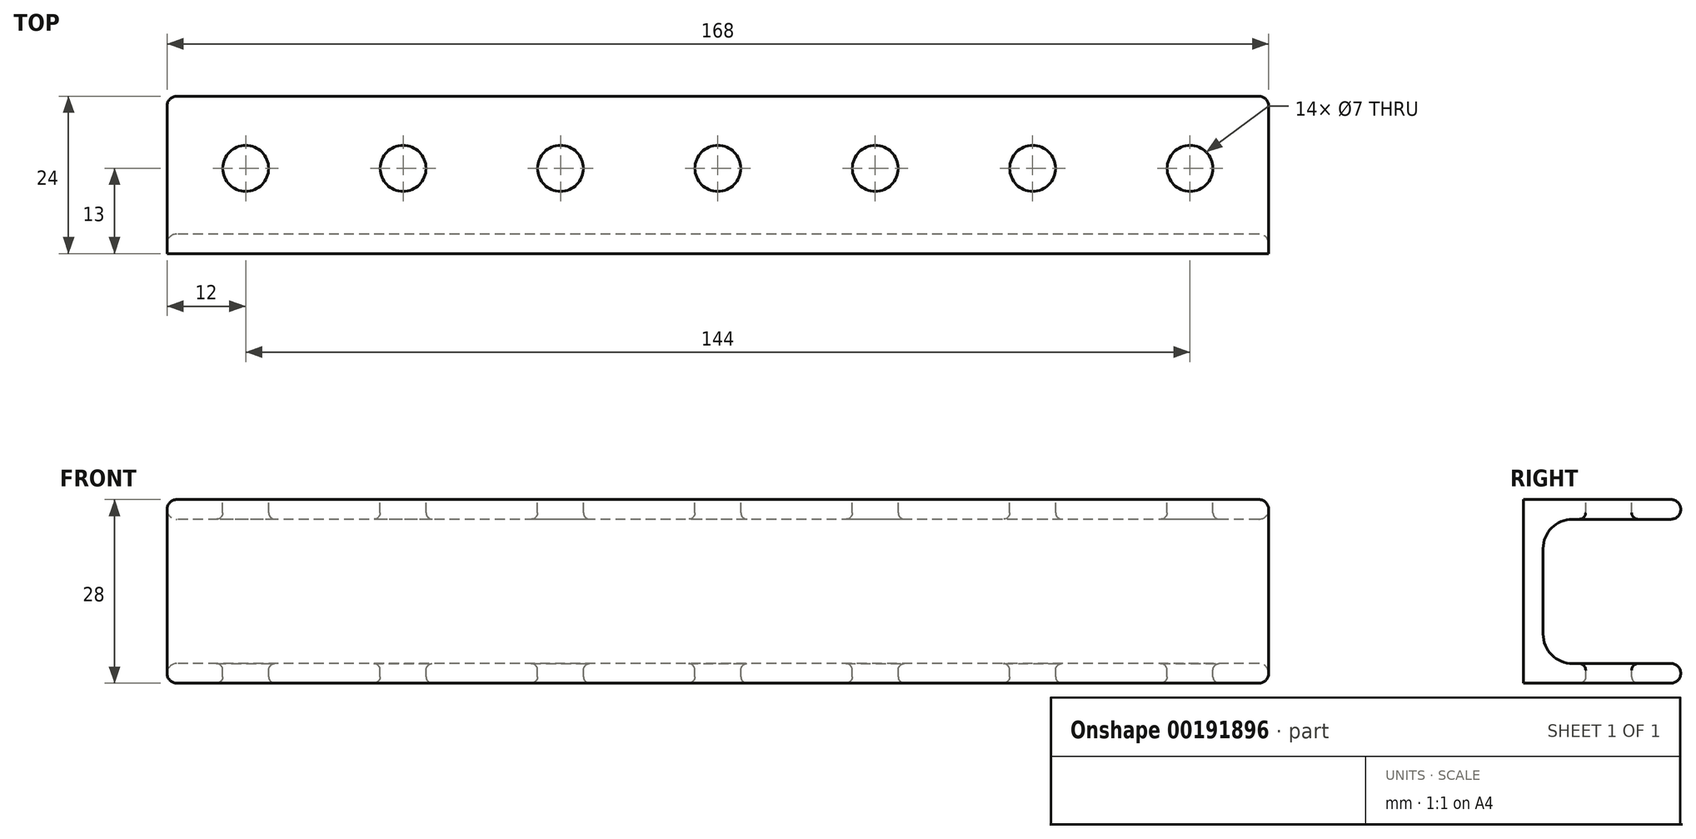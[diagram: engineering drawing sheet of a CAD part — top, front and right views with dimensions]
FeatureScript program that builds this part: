
annotation { "Feature Type Name" : "Feature", "Feature Type Description" : "" }
export const myFeature = defineFeature(function(context is Context, id is Id, definition is map)
    precondition{}
    {
        {
            var Q0;
            Q0=qCreatedBy(makeId("Right.planeOp"),FACE);
            var sketch = newSketch(context, id + "F0", { "sketchPlane" : qUnion([Q0])});
            skLineSegment(sketch, "E0", {"start": v(0, 28) * mm, "end": v(0, 0) * mm});
            skLineSegment(sketch, "E1", {"start": v(0, 0) * mm, "end": v(24, 0) * mm});
            skLineSegment(sketch, "E2", {"start": v(24, 0) * mm, "end": v(24, 3) * mm});
            skLineSegment(sketch, "E3", {"start": v(24, 3) * mm, "end": v(3, 3) * mm});
            skLineSegment(sketch, "E4", {"start": v(3, 3) * mm, "end": v(3, 25) * mm});
            skLineSegment(sketch, "E5", {"start": v(3, 25) * mm, "end": v(24, 25) * mm});
            skLineSegment(sketch, "E6", {"start": v(24, 25) * mm, "end": v(24, 28) * mm});
            skLineSegment(sketch, "E7", {"start": v(24, 28) * mm, "end": v(0, 28) * mm});
            skSolve(sketch);
        }
        {
            var Q0;
            Q0=makeQuery(id+"F0.imprint","IMPRINT",FACE,{"disambiguationData":[TD([[makeQuery(id+"F0.imprint","IMPRINT",EDGE,{"derivedFrom":sQuery(id+"F0.wireOp",EDGE,"E0")}),1.0]])]});
            extrude(context, id + "F1", {"entities" : qUnion([Q0]), "depth" : 168 * mm});
        }
        {
            var Q0;
            Q0=makeQuery(id+"F1.opExtrude","SWEPT_FACE",FACE,{"disambiguationData":[OSD([sQuery(id+"F0.wireOp",EDGE,"E7")])]});
            var sketch = newSketch(context, id + "F2", { "sketchPlane" : qUnion([Q0])});
            skCircle(sketch, "E8", {"center": v(12, 13) * mm, "radius": 3.5 * mm});
            skCircle(sketch, "E9.1.0.0", {"center": v(36, 13) * mm, "radius": 3.5 * mm});
            skCircle(sketch, "E9.2.0.0", {"center": v(60, 13) * mm, "radius": 3.5 * mm});
            skCircle(sketch, "E9.3.0.0", {"center": v(84, 13) * mm, "radius": 3.5 * mm});
            skCircle(sketch, "E9.4.0.0", {"center": v(108, 13) * mm, "radius": 3.5 * mm});
            skCircle(sketch, "E9.5.0.0", {"center": v(132, 13) * mm, "radius": 3.5 * mm});
            skCircle(sketch, "E9.6.0.0", {"center": v(156, 13) * mm, "radius": 3.5 * mm});
            skLineSegment(sketch, "E9.direction1", {"start": v(12, 13) * mm, "end": v(36, 13) * mm, "construction": true});
            skSolve(sketch);
        }
        {
            var Q0;
            Q0=makeQuery(id+"F2.imprint","IMPRINT",FACE,{"disambiguationData":[TD([[makeQuery(id+"F2.imprint","IMPRINT",EDGE,{"derivedFrom":sQuery(id+"F2.wireOp",EDGE,"E8")}),1.0]])]});
            var Q1;
            Q1=makeQuery(id+"F2.imprint","IMPRINT",FACE,{"disambiguationData":[TD([[makeQuery(id+"F2.imprint","IMPRINT",EDGE,{"derivedFrom":sQuery(id+"F2.wireOp",EDGE,"E9.1.0.0")}),1.0]])]});
            var Q2;
            Q2=makeQuery(id+"F2.imprint","IMPRINT",FACE,{"disambiguationData":[TD([[makeQuery(id+"F2.imprint","IMPRINT",EDGE,{"derivedFrom":sQuery(id+"F2.wireOp",EDGE,"E9.2.0.0")}),1.0]])]});
            var Q3;
            Q3=makeQuery(id+"F2.imprint","IMPRINT",FACE,{"disambiguationData":[TD([[makeQuery(id+"F2.imprint","IMPRINT",EDGE,{"derivedFrom":sQuery(id+"F2.wireOp",EDGE,"E9.3.0.0")}),1.0]])]});
            var Q4;
            Q4=makeQuery(id+"F2.imprint","IMPRINT",FACE,{"disambiguationData":[TD([[makeQuery(id+"F2.imprint","IMPRINT",EDGE,{"derivedFrom":sQuery(id+"F2.wireOp",EDGE,"E9.4.0.0")}),1.0]])]});
            var Q5;
            Q5=makeQuery(id+"F2.imprint","IMPRINT",FACE,{"disambiguationData":[TD([[makeQuery(id+"F2.imprint","IMPRINT",EDGE,{"derivedFrom":sQuery(id+"F2.wireOp",EDGE,"E9.5.0.0")}),1.0]])]});
            var Q6;
            Q6=makeQuery(id+"F2.imprint","IMPRINT",FACE,{"disambiguationData":[TD([[makeQuery(id+"F2.imprint","IMPRINT",EDGE,{"derivedFrom":sQuery(id+"F2.wireOp",EDGE,"E9.6.0.0")}),1.0]])]});
            extrude(context, id + "F3", {"entities" : qUnion([Q0, Q1, Q2, Q3, Q4, Q5, Q6]), "operationType" : NewBodyOperationType.REMOVE, "endBound" : BoundingType.THROUGH_ALL, "oppositeDirection" : true, "depth" : 25 * mm});
        }
        {
            var Q0;
            Q0=makeQuery(id+"F1.opExtrude","SWEPT_EDGE",EDGE,{"disambiguationData":[OSD([sQuery(id+"F0.wireOp",EDGE,"E3"),sQuery(id+"F0.wireOp",EDGE,"E4")])]});
            var Q1;
            Q1=makeQuery(id+"F1.opExtrude","SWEPT_EDGE",EDGE,{"disambiguationData":[OSD([sQuery(id+"F0.wireOp",EDGE,"E4"),sQuery(id+"F0.wireOp",EDGE,"E5")])]});
            fillet(context, id + "F4", {"entities" : qUnion([Q0, Q1]), "radius" : 4.5 * mm, "tangentPropagation" : true, "allowEdgeOverflow" : false});
        }
        {
            var Q0;
            Q0=makeQuery(id+"F1.opExtrude","SWEPT_EDGE",EDGE,{"disambiguationData":[OSD([sQuery(id+"F0.wireOp",EDGE,"E2"),sQuery(id+"F0.wireOp",EDGE,"E3")])]});
            var Q1;
            Q1=makeQuery(id+"F1.opExtrude","SWEPT_EDGE",EDGE,{"disambiguationData":[OSD([sQuery(id+"F0.wireOp",EDGE,"E5"),sQuery(id+"F0.wireOp",EDGE,"E6")])]});
            var Q2;
            Q2=makeQuery(id+"F1.opExtrude","SWEPT_EDGE",EDGE,{"disambiguationData":[OSD([sQuery(id+"F0.wireOp",EDGE,"E6"),sQuery(id+"F0.wireOp",EDGE,"E7")])]});
            var Q3;
            Q3=makeQuery(id+"F1.opExtrude","SWEPT_EDGE",EDGE,{"disambiguationData":[OSD([sQuery(id+"F0.wireOp",EDGE,"E1"),sQuery(id+"F0.wireOp",EDGE,"E2")])]});
            var Q4;
            Q4=makeQuery(id+"F1.opExtrude","CAP_EDGE",EDGE,{"disambiguationData":[OSD([sQuery(id+"F0.wireOp",EDGE,"E2")])],"isStart":true});
            var Q5;
            Q5=makeQuery(id+"F1.opExtrude","CAP_EDGE",EDGE,{"disambiguationData":[OSD([sQuery(id+"F0.wireOp",EDGE,"E6")])],"isStart":true});
            var Q6;
            Q6=makeQuery(id+"F1.opExtrude","CAP_EDGE",EDGE,{"disambiguationData":[OSD([sQuery(id+"F0.wireOp",EDGE,"E2")])],"isStart":false});
            var Q7;
            Q7=makeQuery(id+"F1.opExtrude","CAP_EDGE",EDGE,{"disambiguationData":[OSD([sQuery(id+"F0.wireOp",EDGE,"E6")])],"isStart":false});
            var Q8;
            Q8=makeQuery(id+"F1.opExtrude","CAP_EDGE",EDGE,{"disambiguationData":[OSD([sQuery(id+"F0.wireOp",EDGE,"E1")])],"isStart":false});
            var Q9;
            Q9=makeQuery(id+"F1.opExtrude","CAP_EDGE",EDGE,{"disambiguationData":[OSD([sQuery(id+"F0.wireOp",EDGE,"E3")])],"isStart":false});
            var Q10;
            Q10=makeQuery(id+"F1.opExtrude","CAP_EDGE",EDGE,{"disambiguationData":[OSD([sQuery(id+"F0.wireOp",EDGE,"E7")])],"isStart":false});
            var Q11;
            Q11=makeQuery(id+"F1.opExtrude","CAP_EDGE",EDGE,{"disambiguationData":[OSD([sQuery(id+"F0.wireOp",EDGE,"E5")])],"isStart":true});
            var Q12;
            Q12=makeQuery(id+"F1.opExtrude","CAP_EDGE",EDGE,{"disambiguationData":[OSD([sQuery(id+"F0.wireOp",EDGE,"E7")])],"isStart":true});
            var Q13;
            Q13=makeQuery(id+"F1.opExtrude","CAP_EDGE",EDGE,{"disambiguationData":[OSD([sQuery(id+"F0.wireOp",EDGE,"E1")])],"isStart":true});
            fillet(context, id + "F5", {"entities" : qUnion([Q0, Q1, Q2, Q3, Q4, Q5, Q6, Q7, Q8, Q9, Q10, Q11, Q12, Q13]), "radius" : 1.5 * mm, "tangentPropagation" : true, "allowEdgeOverflow" : false});
        }
        {
            var Q0;
            Q0=makeQuery(id+"F3.boolean.opBoolean","COPY",EDGE,{"derivedFrom":makeQuery(id+"F3.opExtrude","CAP_EDGE",EDGE,{"disambiguationData":[OSD([sQuery(id+"F2.wireOp",EDGE,"E8")])],"isStart":true})});
            var Q1;
            Q1=makeQuery(id+"F3.boolean.opBoolean","COPY",EDGE,{"derivedFrom":makeQuery(id+"F3.opExtrude","CAP_EDGE",EDGE,{"disambiguationData":[OSD([sQuery(id+"F2.wireOp",EDGE,"E9.1.0.0")])],"isStart":true})});
            var Q2;
            Q2=makeQuery(id+"F3.boolean.opBoolean","INTERSECT",EDGE,{"derivedFrom":[makeQuery(id+"F1.opExtrude","SWEPT_FACE",FACE,{"disambiguationData":[OSD([sQuery(id+"F0.wireOp",EDGE,"E5")])]}),makeQuery(id+"F3.opExtrude","SWEPT_FACE",FACE,{"disambiguationData":[OSD([sQuery(id+"F2.wireOp",EDGE,"E8")])]})]});
            var Q3;
            Q3=makeQuery(id+"F3.boolean.opBoolean","INTERSECT",EDGE,{"derivedFrom":[makeQuery(id+"F1.opExtrude","SWEPT_FACE",FACE,{"disambiguationData":[OSD([sQuery(id+"F0.wireOp",EDGE,"E5")])]}),makeQuery(id+"F3.opExtrude","SWEPT_FACE",FACE,{"disambiguationData":[OSD([sQuery(id+"F2.wireOp",EDGE,"E9.1.0.0")])]})]});
            var Q4;
            Q4=makeQuery(id+"F3.boolean.opBoolean","COPY",EDGE,{"derivedFrom":makeQuery(id+"F3.opExtrude","CAP_EDGE",EDGE,{"disambiguationData":[OSD([sQuery(id+"F2.wireOp",EDGE,"E9.2.0.0")])],"isStart":true})});
            var Q5;
            Q5=makeQuery(id+"F3.boolean.opBoolean","INTERSECT",EDGE,{"derivedFrom":[makeQuery(id+"F1.opExtrude","SWEPT_FACE",FACE,{"disambiguationData":[OSD([sQuery(id+"F0.wireOp",EDGE,"E5")])]}),makeQuery(id+"F3.opExtrude","SWEPT_FACE",FACE,{"disambiguationData":[OSD([sQuery(id+"F2.wireOp",EDGE,"E9.2.0.0")])]})]});
            var Q6;
            Q6=makeQuery(id+"F3.boolean.opBoolean","COPY",EDGE,{"derivedFrom":makeQuery(id+"F3.opExtrude","CAP_EDGE",EDGE,{"disambiguationData":[OSD([sQuery(id+"F2.wireOp",EDGE,"E9.3.0.0")])],"isStart":true})});
            var Q7;
            Q7=makeQuery(id+"F3.boolean.opBoolean","INTERSECT",EDGE,{"derivedFrom":[makeQuery(id+"F1.opExtrude","SWEPT_FACE",FACE,{"disambiguationData":[OSD([sQuery(id+"F0.wireOp",EDGE,"E5")])]}),makeQuery(id+"F3.opExtrude","SWEPT_FACE",FACE,{"disambiguationData":[OSD([sQuery(id+"F2.wireOp",EDGE,"E9.3.0.0")])]})]});
            var Q8;
            Q8=makeQuery(id+"F3.boolean.opBoolean","COPY",EDGE,{"derivedFrom":makeQuery(id+"F3.opExtrude","CAP_EDGE",EDGE,{"disambiguationData":[OSD([sQuery(id+"F2.wireOp",EDGE,"E9.4.0.0")])],"isStart":true})});
            var Q9;
            Q9=makeQuery(id+"F3.boolean.opBoolean","INTERSECT",EDGE,{"derivedFrom":[makeQuery(id+"F1.opExtrude","SWEPT_FACE",FACE,{"disambiguationData":[OSD([sQuery(id+"F0.wireOp",EDGE,"E5")])]}),makeQuery(id+"F3.opExtrude","SWEPT_FACE",FACE,{"disambiguationData":[OSD([sQuery(id+"F2.wireOp",EDGE,"E9.4.0.0")])]})]});
            var Q10;
            Q10=makeQuery(id+"F3.boolean.opBoolean","COPY",EDGE,{"derivedFrom":makeQuery(id+"F3.opExtrude","CAP_EDGE",EDGE,{"disambiguationData":[OSD([sQuery(id+"F2.wireOp",EDGE,"E9.5.0.0")])],"isStart":true})});
            var Q11;
            Q11=makeQuery(id+"F3.boolean.opBoolean","INTERSECT",EDGE,{"derivedFrom":[makeQuery(id+"F1.opExtrude","SWEPT_FACE",FACE,{"disambiguationData":[OSD([sQuery(id+"F0.wireOp",EDGE,"E1")])]}),makeQuery(id+"F3.opExtrude","SWEPT_FACE",FACE,{"disambiguationData":[OSD([sQuery(id+"F2.wireOp",EDGE,"E8")])]})]});
            var Q12;
            Q12=makeQuery(id+"F3.boolean.opBoolean","INTERSECT",EDGE,{"derivedFrom":[makeQuery(id+"F1.opExtrude","SWEPT_FACE",FACE,{"disambiguationData":[OSD([sQuery(id+"F0.wireOp",EDGE,"E1")])]}),makeQuery(id+"F3.opExtrude","SWEPT_FACE",FACE,{"disambiguationData":[OSD([sQuery(id+"F2.wireOp",EDGE,"E9.1.0.0")])]})]});
            var Q13;
            Q13=makeQuery(id+"F3.boolean.opBoolean","INTERSECT",EDGE,{"derivedFrom":[makeQuery(id+"F1.opExtrude","SWEPT_FACE",FACE,{"disambiguationData":[OSD([sQuery(id+"F0.wireOp",EDGE,"E3")])]}),makeQuery(id+"F3.opExtrude","SWEPT_FACE",FACE,{"disambiguationData":[OSD([sQuery(id+"F2.wireOp",EDGE,"E9.1.0.0")])]})]});
            var Q14;
            Q14=makeQuery(id+"F3.boolean.opBoolean","INTERSECT",EDGE,{"derivedFrom":[makeQuery(id+"F1.opExtrude","SWEPT_FACE",FACE,{"disambiguationData":[OSD([sQuery(id+"F0.wireOp",EDGE,"E3")])]}),makeQuery(id+"F3.opExtrude","SWEPT_FACE",FACE,{"disambiguationData":[OSD([sQuery(id+"F2.wireOp",EDGE,"E8")])]})]});
            var Q15;
            Q15=makeQuery(id+"F3.boolean.opBoolean","INTERSECT",EDGE,{"derivedFrom":[makeQuery(id+"F1.opExtrude","SWEPT_FACE",FACE,{"disambiguationData":[OSD([sQuery(id+"F0.wireOp",EDGE,"E1")])]}),makeQuery(id+"F3.opExtrude","SWEPT_FACE",FACE,{"disambiguationData":[OSD([sQuery(id+"F2.wireOp",EDGE,"E9.2.0.0")])]})]});
            var Q16;
            Q16=makeQuery(id+"F3.boolean.opBoolean","INTERSECT",EDGE,{"derivedFrom":[makeQuery(id+"F1.opExtrude","SWEPT_FACE",FACE,{"disambiguationData":[OSD([sQuery(id+"F0.wireOp",EDGE,"E1")])]}),makeQuery(id+"F3.opExtrude","SWEPT_FACE",FACE,{"disambiguationData":[OSD([sQuery(id+"F2.wireOp",EDGE,"E9.3.0.0")])]})]});
            var Q17;
            Q17=makeQuery(id+"F3.boolean.opBoolean","INTERSECT",EDGE,{"derivedFrom":[makeQuery(id+"F1.opExtrude","SWEPT_FACE",FACE,{"disambiguationData":[OSD([sQuery(id+"F0.wireOp",EDGE,"E1")])]}),makeQuery(id+"F3.opExtrude","SWEPT_FACE",FACE,{"disambiguationData":[OSD([sQuery(id+"F2.wireOp",EDGE,"E9.4.0.0")])]})]});
            var Q18;
            Q18=makeQuery(id+"F3.boolean.opBoolean","INTERSECT",EDGE,{"derivedFrom":[makeQuery(id+"F1.opExtrude","SWEPT_FACE",FACE,{"disambiguationData":[OSD([sQuery(id+"F0.wireOp",EDGE,"E1")])]}),makeQuery(id+"F3.opExtrude","SWEPT_FACE",FACE,{"disambiguationData":[OSD([sQuery(id+"F2.wireOp",EDGE,"E9.5.0.0")])]})]});
            var Q19;
            Q19=makeQuery(id+"F3.boolean.opBoolean","INTERSECT",EDGE,{"derivedFrom":[makeQuery(id+"F1.opExtrude","SWEPT_FACE",FACE,{"disambiguationData":[OSD([sQuery(id+"F0.wireOp",EDGE,"E1")])]}),makeQuery(id+"F3.opExtrude","SWEPT_FACE",FACE,{"disambiguationData":[OSD([sQuery(id+"F2.wireOp",EDGE,"E9.6.0.0")])]})]});
            var Q20;
            Q20=makeQuery(id+"F3.boolean.opBoolean","INTERSECT",EDGE,{"derivedFrom":[makeQuery(id+"F1.opExtrude","SWEPT_FACE",FACE,{"disambiguationData":[OSD([sQuery(id+"F0.wireOp",EDGE,"E3")])]}),makeQuery(id+"F3.opExtrude","SWEPT_FACE",FACE,{"disambiguationData":[OSD([sQuery(id+"F2.wireOp",EDGE,"E9.2.0.0")])]})]});
            var Q21;
            Q21=makeQuery(id+"F3.boolean.opBoolean","INTERSECT",EDGE,{"derivedFrom":[makeQuery(id+"F1.opExtrude","SWEPT_FACE",FACE,{"disambiguationData":[OSD([sQuery(id+"F0.wireOp",EDGE,"E3")])]}),makeQuery(id+"F3.opExtrude","SWEPT_FACE",FACE,{"disambiguationData":[OSD([sQuery(id+"F2.wireOp",EDGE,"E9.3.0.0")])]})]});
            var Q22;
            Q22=makeQuery(id+"F3.boolean.opBoolean","INTERSECT",EDGE,{"derivedFrom":[makeQuery(id+"F1.opExtrude","SWEPT_FACE",FACE,{"disambiguationData":[OSD([sQuery(id+"F0.wireOp",EDGE,"E3")])]}),makeQuery(id+"F3.opExtrude","SWEPT_FACE",FACE,{"disambiguationData":[OSD([sQuery(id+"F2.wireOp",EDGE,"E9.4.0.0")])]})]});
            var Q23;
            Q23=makeQuery(id+"F3.boolean.opBoolean","INTERSECT",EDGE,{"derivedFrom":[makeQuery(id+"F1.opExtrude","SWEPT_FACE",FACE,{"disambiguationData":[OSD([sQuery(id+"F0.wireOp",EDGE,"E3")])]}),makeQuery(id+"F3.opExtrude","SWEPT_FACE",FACE,{"disambiguationData":[OSD([sQuery(id+"F2.wireOp",EDGE,"E9.5.0.0")])]})]});
            var Q24;
            Q24=makeQuery(id+"F3.boolean.opBoolean","INTERSECT",EDGE,{"derivedFrom":[makeQuery(id+"F1.opExtrude","SWEPT_FACE",FACE,{"disambiguationData":[OSD([sQuery(id+"F0.wireOp",EDGE,"E3")])]}),makeQuery(id+"F3.opExtrude","SWEPT_FACE",FACE,{"disambiguationData":[OSD([sQuery(id+"F2.wireOp",EDGE,"E9.6.0.0")])]})]});
            var Q25;
            Q25=makeQuery(id+"F3.boolean.opBoolean","INTERSECT",EDGE,{"derivedFrom":[makeQuery(id+"F1.opExtrude","SWEPT_FACE",FACE,{"disambiguationData":[OSD([sQuery(id+"F0.wireOp",EDGE,"E5")])]}),makeQuery(id+"F3.opExtrude","SWEPT_FACE",FACE,{"disambiguationData":[OSD([sQuery(id+"F2.wireOp",EDGE,"E9.5.0.0")])]})]});
            var Q26;
            Q26=makeQuery(id+"F3.boolean.opBoolean","INTERSECT",EDGE,{"derivedFrom":[makeQuery(id+"F1.opExtrude","SWEPT_FACE",FACE,{"disambiguationData":[OSD([sQuery(id+"F0.wireOp",EDGE,"E5")])]}),makeQuery(id+"F3.opExtrude","SWEPT_FACE",FACE,{"disambiguationData":[OSD([sQuery(id+"F2.wireOp",EDGE,"E9.6.0.0")])]})]});
            var Q27;
            Q27=makeQuery(id+"F3.boolean.opBoolean","COPY",EDGE,{"derivedFrom":makeQuery(id+"F3.opExtrude","CAP_EDGE",EDGE,{"disambiguationData":[OSD([sQuery(id+"F2.wireOp",EDGE,"E9.6.0.0")])],"isStart":true})});
            fillet(context, id + "F6", {"entities" : qUnion([Q0, Q1, Q2, Q3, Q4, Q5, Q6, Q7, Q8, Q9, Q10, Q11, Q12, Q13, Q14, Q15, Q16, Q17, Q18, Q19, Q20, Q21, Q22, Q23, Q24, Q25, Q26, Q27]), "radius" : 1 * mm, "tangentPropagation" : true, "allowEdgeOverflow" : false});
        }
    });
